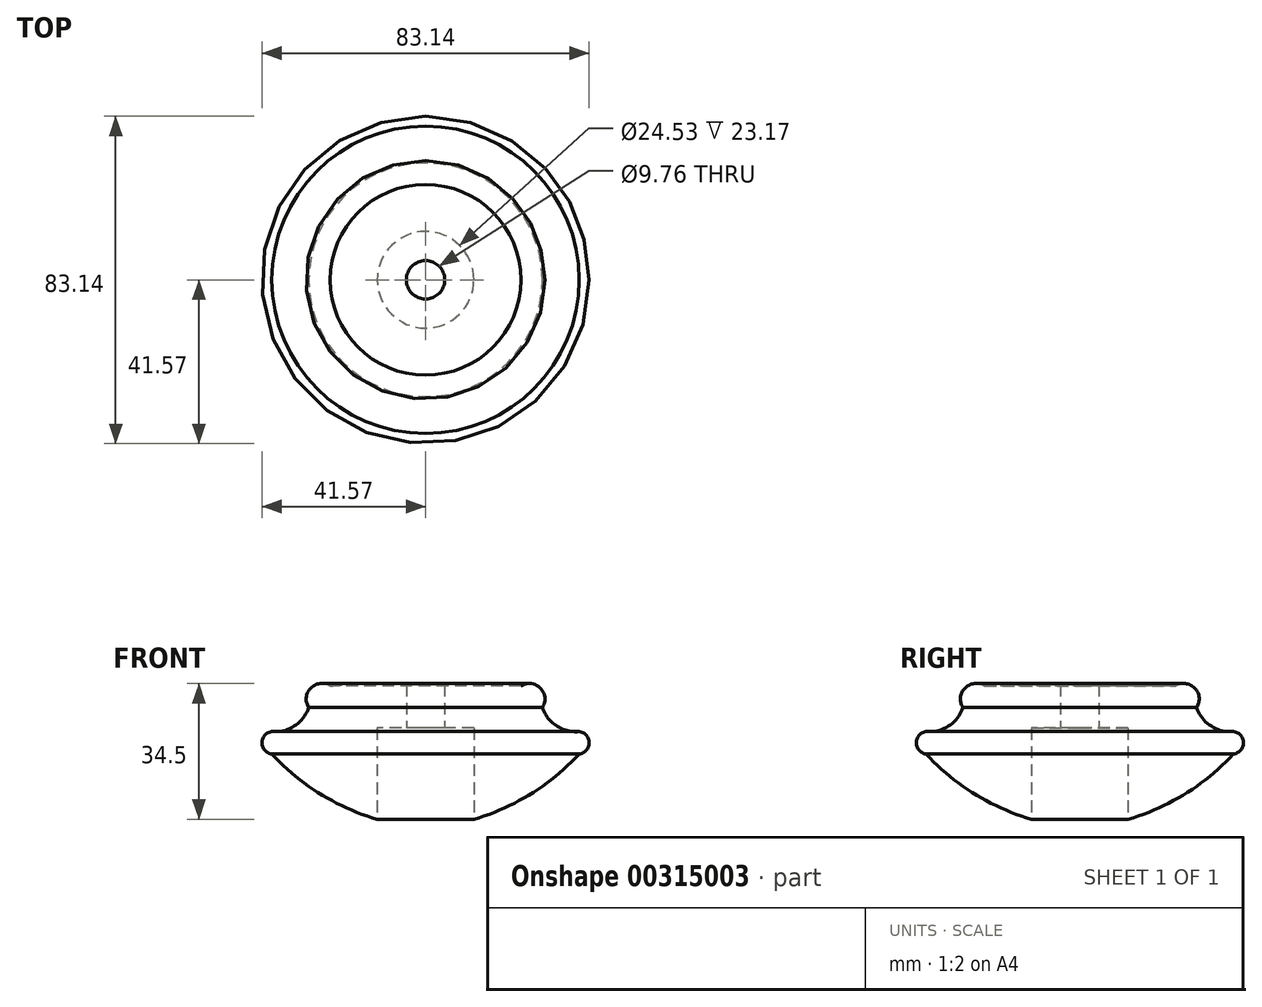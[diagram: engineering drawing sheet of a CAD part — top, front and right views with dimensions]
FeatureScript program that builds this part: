
annotation { "Feature Type Name" : "Feature", "Feature Type Description" : "" }
export const myFeature = defineFeature(function(context is Context, id is Id, definition is map)
    precondition{}
    {
        {
            var Q0;
            Q0=qCreatedBy(makeId("Front.planeOp"),FACE);
            var sketch = newSketch(context, id + "F0", { "sketchPlane" : qUnion([Q0])});
            skArc(sketch, "E0", {"start": v(-40, 19.87) * mm, "mid": v(-21.94, 6.02) * mm, "end": v(0, 0) * mm});
            skLineSegment(sketch, "E1", {"start": v(-18.7, 36.46) * mm, "end": v(0, 36.46) * mm});
            skLineSegment(sketch, "E2", {"start": v(0, 36.46) * mm, "end": v(0, 0) * mm});
            skArc(sketch, "E3", {"start": v(-18.7, 36.46) * mm, "mid": v(-21.48, 36.36) * mm, "end": v(-24.24, 36.07) * mm});
            skArc(sketch, "E4", {"start": v(-41.42, 22.6) * mm, "mid": v(-40.48, 20.57) * mm, "end": v(-39.06, 18.84) * mm});
            skArc(sketch, "E5", {"start": v(-39.05, 24.52) * mm, "mid": v(-33.3, 25.95) * mm, "end": v(-29.67, 30.63) * mm});
            skPoint(sketch, "E5.endSnap0", {"position": v(-29.67, 34.98) * mm});
            skArc(sketch, "E6", {"start": v(-24.24, 36.07) * mm, "mid": v(-29.18, 35.57) * mm, "end": v(-29.67, 30.63) * mm});
            skArc(sketch, "E7", {"start": v(-39.05, 24.52) * mm, "mid": v(-39.06, 24.87) * mm, "end": v(-39.06, 25.22) * mm});
            skArc(sketch, "E8", {"start": v(-39.05, 24.52) * mm, "mid": v(-41.57, 21.69) * mm, "end": v(-39.06, 18.84) * mm});
            skPoint(sketch, "E9.orphan", {"position": v(-41.81, 25.22) * mm});
            skArc(sketch, "E10.trimOffspring", {"start": v(-29.32, 35.07) * mm, "mid": v(-29.5, 35.02) * mm, "end": v(-29.67, 34.98) * mm});
            skArc(sketch, "E11.trimOffspring", {"start": v(-29.32, 35.07) * mm, "mid": v(-29.46, 35.77) * mm, "end": v(-29.67, 36.46) * mm});
            skSolve(sketch);
        }
        {
            var Q0;
            Q0 = qSketchRegion(id + "F0", true);
            var Q1;
            Q1=sQuery(id+"F0.wireOp",EDGE,"E2");
            revolve(context, id + "F1", {"entities" : qUnion([Q0]), "axis" : qUnion([Q1]), "revolveType" : RevolveType.FULL});
        }
        {
            var Q0;
            Q0=qCreatedBy(makeId("Top.planeOp"),FACE);
            var sketch = newSketch(context, id + "F2", { "sketchPlane" : qUnion([Q0])});
            skCircle(sketch, "E12", {"center": v(0, 0) * mm, "radius": 12.26 * mm});
            skSolve(sketch);
        }
        {
            var Q0;
            Q0 = qSketchRegion(id + "F2", true);
            extrude(context, id + "F3", {"entities" : qUnion([Q0]), "operationType" : NewBodyOperationType.REMOVE, "depth" : 25.4 * mm});
        }
        {
            var Q0;
            Q0=qCreatedBy(makeId("Top.planeOp"),FACE);
            var sketch = newSketch(context, id + "F4", { "sketchPlane" : qUnion([Q0])});
            skCircle(sketch, "E13", {"center": v(0, 0) * mm, "radius": 4.88 * mm});
            skSolve(sketch);
        }
        {
            var Q0;
            Q0 = qSketchRegion(id + "F4", true);
            extrude(context, id + "F5", {"entities" : qUnion([Q0]), "operationType" : NewBodyOperationType.REMOVE, "depth" : 62.74 * mm});
        }
    });
